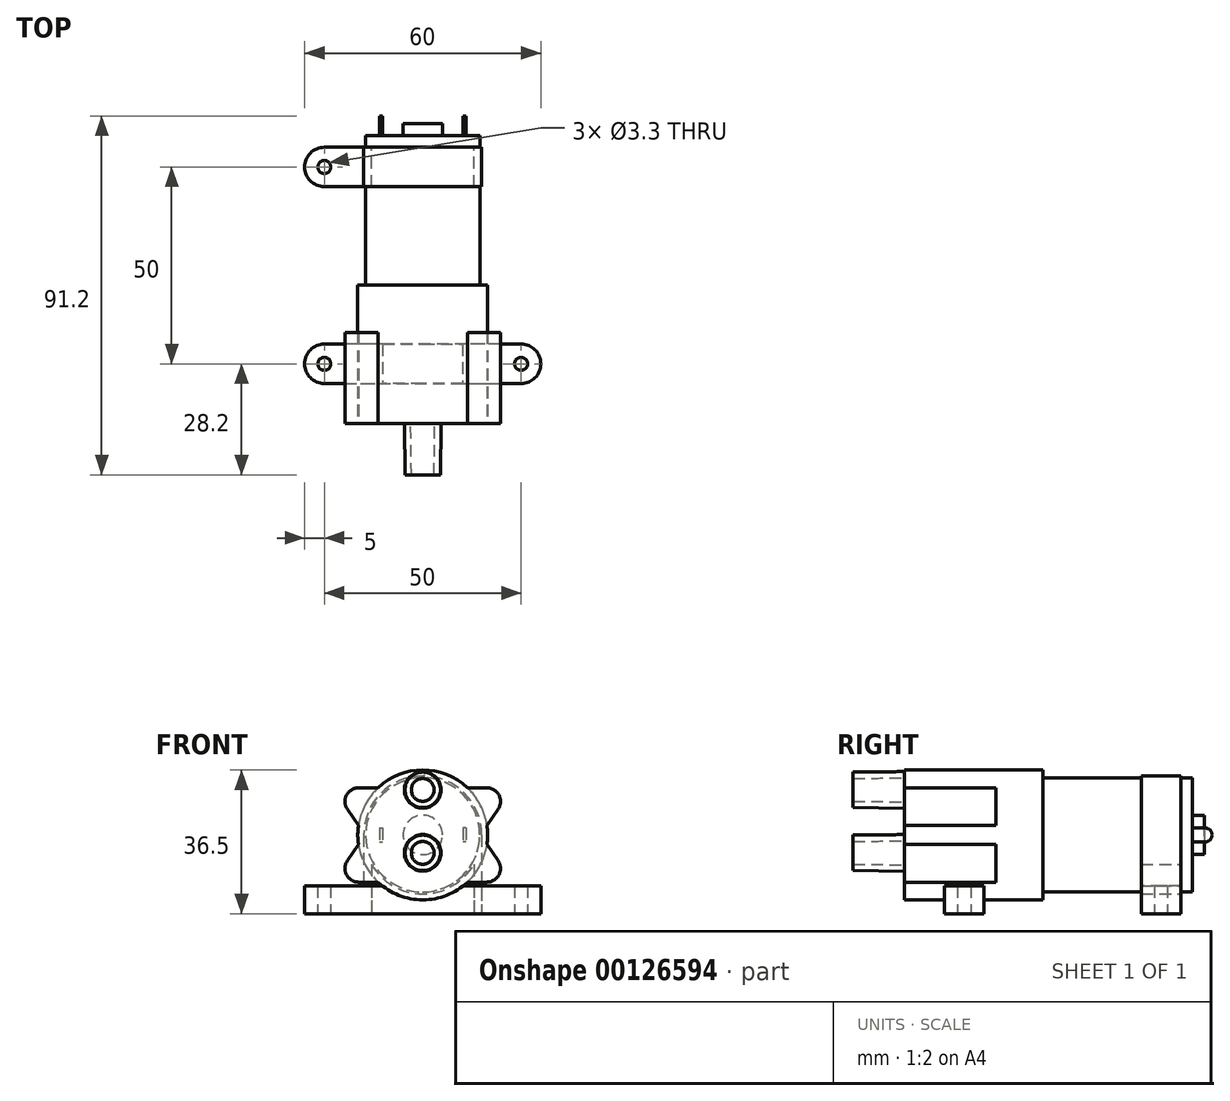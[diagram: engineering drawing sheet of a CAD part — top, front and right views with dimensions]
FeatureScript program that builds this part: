
annotation { "Feature Type Name" : "Feature", "Feature Type Description" : "" }
export const myFeature = defineFeature(function(context is Context, id is Id, definition is map)
    precondition{}
    {
        {
            var Q0;
            Q0=qCreatedBy(makeId("Front.planeOp"),FACE);
            var sketch = newSketch(context, id + "F0", { "sketchPlane" : qUnion([Q0])});
            skCircle(sketch, "E0", {"center": v(0, 0) * mm, "radius": 16.5 * mm});
            skCircle(sketch, "E1", {"center": v(16.25, -8.5) * mm, "radius": 3.5 * mm});
            skCircle(sketch, "E2.0.1.0", {"center": v(16.25, 8.5) * mm, "radius": 3.5 * mm});
            skCircle(sketch, "E2.1.0.0", {"center": v(-16.25, -8.5) * mm, "radius": 3.5 * mm});
            skCircle(sketch, "E2.1.1.0", {"center": v(-16.25, 8.5) * mm, "radius": 3.5 * mm});
            skLineSegment(sketch, "E2.direction1", {"start": v(16.25, -8.5) * mm, "end": v(-16.25, -8.5) * mm, "construction": true});
            skLineSegment(sketch, "E2.direction2", {"start": v(16.25, -8.5) * mm, "end": v(16.25, 8.5) * mm, "construction": true});
            skLineSegment(sketch, "E3", {"start": v(16.25, -8.5) * mm, "end": v(-16.25, 8.5) * mm, "construction": true});
            skLineSegment(sketch, "E4", {"start": v(16.25, 8.5) * mm, "end": v(-16.25, -8.5) * mm, "construction": true});
            skLineSegment(sketch, "E5", {"start": v(16.25, -12) * mm, "end": v(-16.25, -12) * mm});
            skLineSegment(sketch, "E6.MirrorCS", {"start": v(19.12, -6.5) * mm, "end": v(16.25, -2.36) * mm});
            skLineSegment(sketch, "E7.MirrorCS", {"start": v(-19.12, -6.5) * mm, "end": v(-16.25, -2.36) * mm});
            skLineSegment(sketch, "E8.MirrorCS", {"start": v(-19.12, 6.5) * mm, "end": v(-16.25, 2.36) * mm});
            skLineSegment(sketch, "E9.MirrorCS", {"start": v(19.12, 6.5) * mm, "end": v(16.25, 2.36) * mm});
            skLineSegment(sketch, "E10.MirrorCS", {"start": v(16.25, 12) * mm, "end": v(-16.25, 12) * mm});
            skSolve(sketch);
        }
        {
            var Q0;
            {var subQ0=sQuery(id+"F0.wireOp",EDGE,"E0");var subQ16=makeQuery(id+"F0.imprint","INTERSECT",VERTEX,{"derivedFrom":[subQ0,sQuery(id+"F0.wireOp",EDGE,"E9.MirrorCS")]});Q0=makeQuery(id+"F0.imprint","IMPRINT",FACE,{"disambiguationData":[TD([[makeQuery(id+"F0.imprint","IMPRINT",EDGE,{"disambiguationData":[TD([[subQ16,-1.0]])],"derivedFrom":subQ0}),1.0]])]});}
            var Q1;
            {var subQ0=sQuery(id+"F0.wireOp",EDGE,"E10.MirrorCS");var subQ1=sQuery(id+"F0.wireOp",EDGE,"E0");var subQ2=makeQuery(id+"F0.imprint","INTERSECT",VERTEX,{"disambiguationData":[OD(0.0)],"derivedFrom":[subQ1,subQ0]});Q1=makeQuery(id+"F0.imprint","IMPRINT",FACE,{"disambiguationData":[TD([[makeQuery(id+"F0.imprint","IMPRINT",EDGE,{"disambiguationData":[TD([[subQ2,1.0]])],"derivedFrom":subQ1}),-1.0]])]});}
            var Q2;
            {var subQ0=sQuery(id+"F0.wireOp",EDGE,"E2.1.1.0");var subQ1=sQuery(id+"F0.wireOp",EDGE,"E0");var subQ2=makeQuery(id+"F0.imprint","INTERSECT",VERTEX,{"disambiguationData":[OD(0.0)],"derivedFrom":[subQ1,subQ0]});Q2=makeQuery(id+"F0.imprint","IMPRINT",FACE,{"disambiguationData":[TD([[makeQuery(id+"F0.imprint","IMPRINT",EDGE,{"disambiguationData":[TD([[subQ2,-1.0]])],"derivedFrom":subQ1}),1.0]])]});}
            var Q3;
            {var subQ0=sQuery(id+"F0.wireOp",EDGE,"E2.1.1.0");var subQ1=sQuery(id+"F0.wireOp",EDGE,"E0");var subQ2=makeQuery(id+"F0.imprint","INTERSECT",VERTEX,{"disambiguationData":[OD(0.0)],"derivedFrom":[subQ1,subQ0]});Q3=makeQuery(id+"F0.imprint","IMPRINT",FACE,{"disambiguationData":[TD([[makeQuery(id+"F0.imprint","IMPRINT",EDGE,{"disambiguationData":[TD([[subQ2,-1.0]])],"derivedFrom":subQ1}),-1.0]])]});}
            var Q4;
            {var subQ0=sQuery(id+"F0.wireOp",EDGE,"E5");var subQ1=sQuery(id+"F0.wireOp",EDGE,"E0");var subQ2=makeQuery(id+"F0.imprint","INTERSECT",VERTEX,{"disambiguationData":[OD(0.0)],"derivedFrom":[subQ1,subQ0]});Q4=makeQuery(id+"F0.imprint","IMPRINT",FACE,{"disambiguationData":[TD([[makeQuery(id+"F0.imprint","IMPRINT",EDGE,{"disambiguationData":[TD([[subQ2,1.0]])],"derivedFrom":subQ1}),-1.0]])]});}
            var Q5;
            {var subQ0=sQuery(id+"F0.wireOp",EDGE,"E10.MirrorCS");var subQ1=sQuery(id+"F0.wireOp",EDGE,"E0");var subQ2=makeQuery(id+"F0.imprint","INTERSECT",VERTEX,{"disambiguationData":[OD(0.0)],"derivedFrom":[subQ1,subQ0]});Q5=makeQuery(id+"F0.imprint","IMPRINT",FACE,{"disambiguationData":[TD([[makeQuery(id+"F0.imprint","IMPRINT",EDGE,{"disambiguationData":[TD([[subQ2,-1.0]])],"derivedFrom":subQ1}),1.0]])]});}
            var Q6;
            {var subQ0=sQuery(id+"F0.wireOp",EDGE,"E6.MirrorCS");var subQ1=sQuery(id+"F0.wireOp",EDGE,"E0");var subQ2=makeQuery(id+"F0.imprint","INTERSECT",VERTEX,{"derivedFrom":[subQ1,subQ0]});Q6=makeQuery(id+"F0.imprint","IMPRINT",FACE,{"disambiguationData":[TD([[makeQuery(id+"F0.imprint","IMPRINT",EDGE,{"disambiguationData":[TD([[subQ2,1.0]])],"derivedFrom":subQ1}),-1.0]])]});}
            var Q7;
            {var subQ0=sQuery(id+"F0.wireOp",EDGE,"E2.0.1.0");var subQ1=sQuery(id+"F0.wireOp",EDGE,"E0");var subQ2=makeQuery(id+"F0.imprint","INTERSECT",VERTEX,{"disambiguationData":[OD(0.0)],"derivedFrom":[subQ1,subQ0]});Q7=makeQuery(id+"F0.imprint","IMPRINT",FACE,{"disambiguationData":[TD([[makeQuery(id+"F0.imprint","IMPRINT",EDGE,{"disambiguationData":[TD([[subQ2,-1.0]])],"derivedFrom":subQ1}),-1.0]])]});}
            var Q8;
            {var subQ0=sQuery(id+"F0.wireOp",EDGE,"E2.1.0.0");var subQ1=sQuery(id+"F0.wireOp",EDGE,"E0");var subQ2=makeQuery(id+"F0.imprint","INTERSECT",VERTEX,{"disambiguationData":[OD(0.0)],"derivedFrom":[subQ1,subQ0]});Q8=makeQuery(id+"F0.imprint","IMPRINT",FACE,{"disambiguationData":[TD([[makeQuery(id+"F0.imprint","IMPRINT",EDGE,{"disambiguationData":[TD([[subQ2,-1.0]])],"derivedFrom":subQ1}),-1.0]])]});}
            var Q9;
            {var subQ0=sQuery(id+"F0.wireOp",EDGE,"E5");var subQ1=sQuery(id+"F0.wireOp",EDGE,"E0");var subQ2=makeQuery(id+"F0.imprint","INTERSECT",VERTEX,{"disambiguationData":[OD(1.0)],"derivedFrom":[subQ1,subQ0]});Q9=makeQuery(id+"F0.imprint","IMPRINT",FACE,{"disambiguationData":[TD([[makeQuery(id+"F0.imprint","IMPRINT",EDGE,{"disambiguationData":[TD([[subQ2,-1.0]])],"derivedFrom":subQ1}),-1.0]])]});}
            var Q10;
            {var subQ0=sQuery(id+"F0.wireOp",EDGE,"E1");var subQ1=sQuery(id+"F0.wireOp",EDGE,"E0");var subQ2=makeQuery(id+"F0.imprint","INTERSECT",VERTEX,{"disambiguationData":[OD(0.0)],"derivedFrom":[subQ1,subQ0]});Q10=makeQuery(id+"F0.imprint","IMPRINT",FACE,{"disambiguationData":[TD([[makeQuery(id+"F0.imprint","IMPRINT",EDGE,{"disambiguationData":[TD([[subQ2,-1.0]])],"derivedFrom":subQ1}),-1.0]])]});}
            var Q11;
            {var subQ0=sQuery(id+"F0.wireOp",EDGE,"E10.MirrorCS");var subQ1=sQuery(id+"F0.wireOp",EDGE,"E0");var subQ2=makeQuery(id+"F0.imprint","INTERSECT",VERTEX,{"disambiguationData":[OD(1.0)],"derivedFrom":[subQ1,subQ0]});Q11=makeQuery(id+"F0.imprint","IMPRINT",FACE,{"disambiguationData":[TD([[makeQuery(id+"F0.imprint","IMPRINT",EDGE,{"disambiguationData":[TD([[subQ2,-1.0]])],"derivedFrom":subQ1}),-1.0]])]});}
            var Q12;
            {var subQ0=sQuery(id+"F0.wireOp",EDGE,"E9.MirrorCS");var subQ1=sQuery(id+"F0.wireOp",EDGE,"E0");var subQ2=makeQuery(id+"F0.imprint","INTERSECT",VERTEX,{"derivedFrom":[subQ1,subQ0]});Q12=makeQuery(id+"F0.imprint","IMPRINT",FACE,{"disambiguationData":[TD([[makeQuery(id+"F0.imprint","IMPRINT",EDGE,{"disambiguationData":[TD([[subQ2,-1.0]])],"derivedFrom":subQ1}),-1.0]])]});}
            var Q13;
            {var subQ0=sQuery(id+"F0.wireOp",EDGE,"E2.0.1.0");var subQ1=sQuery(id+"F0.wireOp",EDGE,"E0");var subQ2=makeQuery(id+"F0.imprint","INTERSECT",VERTEX,{"disambiguationData":[OD(0.0)],"derivedFrom":[subQ1,subQ0]});Q13=makeQuery(id+"F0.imprint","IMPRINT",FACE,{"disambiguationData":[TD([[makeQuery(id+"F0.imprint","IMPRINT",EDGE,{"disambiguationData":[TD([[subQ2,-1.0]])],"derivedFrom":subQ1}),1.0]])]});}
            var Q14;
            {var subQ0=sQuery(id+"F0.wireOp",EDGE,"E1");var subQ1=sQuery(id+"F0.wireOp",EDGE,"E0");var subQ2=makeQuery(id+"F0.imprint","INTERSECT",VERTEX,{"disambiguationData":[OD(0.0)],"derivedFrom":[subQ1,subQ0]});Q14=makeQuery(id+"F0.imprint","IMPRINT",FACE,{"disambiguationData":[TD([[makeQuery(id+"F0.imprint","IMPRINT",EDGE,{"disambiguationData":[TD([[subQ2,-1.0]])],"derivedFrom":subQ1}),1.0]])]});}
            var Q15;
            {var subQ0=sQuery(id+"F0.wireOp",EDGE,"E7.MirrorCS");var subQ1=sQuery(id+"F0.wireOp",EDGE,"E0");var subQ2=makeQuery(id+"F0.imprint","INTERSECT",VERTEX,{"derivedFrom":[subQ1,subQ0]});Q15=makeQuery(id+"F0.imprint","IMPRINT",FACE,{"disambiguationData":[TD([[makeQuery(id+"F0.imprint","IMPRINT",EDGE,{"disambiguationData":[TD([[subQ2,-1.0]])],"derivedFrom":subQ1}),-1.0]])]});}
            var Q16;
            {var subQ0=sQuery(id+"F0.wireOp",EDGE,"E2.1.0.0");var subQ1=sQuery(id+"F0.wireOp",EDGE,"E0");var subQ2=makeQuery(id+"F0.imprint","INTERSECT",VERTEX,{"disambiguationData":[OD(0.0)],"derivedFrom":[subQ1,subQ0]});Q16=makeQuery(id+"F0.imprint","IMPRINT",FACE,{"disambiguationData":[TD([[makeQuery(id+"F0.imprint","IMPRINT",EDGE,{"disambiguationData":[TD([[subQ2,-1.0]])],"derivedFrom":subQ1}),1.0]])]});}
            var Q17;
            {var subQ0=sQuery(id+"F0.wireOp",EDGE,"E8.MirrorCS");var subQ1=sQuery(id+"F0.wireOp",EDGE,"E0");var subQ2=makeQuery(id+"F0.imprint","INTERSECT",VERTEX,{"derivedFrom":[subQ1,subQ0]});Q17=makeQuery(id+"F0.imprint","IMPRINT",FACE,{"disambiguationData":[TD([[makeQuery(id+"F0.imprint","IMPRINT",EDGE,{"disambiguationData":[TD([[subQ2,1.0]])],"derivedFrom":subQ1}),-1.0]])]});}
            var Q18;
            {var subQ0=sQuery(id+"F0.wireOp",EDGE,"E5");var subQ1=sQuery(id+"F0.wireOp",EDGE,"E0");var subQ2=makeQuery(id+"F0.imprint","INTERSECT",VERTEX,{"disambiguationData":[OD(0.0)],"derivedFrom":[subQ1,subQ0]});Q18=makeQuery(id+"F0.imprint","IMPRINT",FACE,{"disambiguationData":[TD([[makeQuery(id+"F0.imprint","IMPRINT",EDGE,{"disambiguationData":[TD([[subQ2,-1.0]])],"derivedFrom":subQ1}),1.0]])]});}
            extrude(context, id + "F1", {"entities" : qUnion([Q0, Q1, Q2, Q3, Q4, Q5, Q6, Q7, Q8, Q9, Q10, Q11, Q12, Q13, Q14, Q15, Q16, Q17, Q18]), "oppositeDirection" : true, "depth" : 23.2 * mm, "offsetDistance" : 25 * mm});
        }
        {
            var Q0;
            Q0=qCreatedBy(makeId("Right.planeOp"),FACE);
            var sketch = newSketch(context, id + "F2", { "sketchPlane" : qUnion([Q0])});
            skLineSegment(sketch, "E11", {"start": v(0, 11.45) * mm, "end": v(-13, 11.45) * mm, "construction": true});
            skLineSegment(sketch, "E12", {"start": v(0, 16.1) * mm, "end": v(-13, 15.95) * mm});
            skLineSegment(sketch, "E13", {"start": v(-13, 15.95) * mm, "end": v(-12.98, 14.35) * mm});
            skLineSegment(sketch, "E14", {"start": v(-12.98, 14.35) * mm, "end": v(0, 14.5) * mm});
            skLineSegment(sketch, "E15", {"start": v(0, 16.1) * mm, "end": v(0, 14.5) * mm});
            skLineSegment(sketch, "E16.0.1.0", {"start": v(0, 0.1) * mm, "end": v(0, -1.5) * mm});
            skLineSegment(sketch, "E16.0.1.1", {"start": v(-12.98, -1.65) * mm, "end": v(0, -1.5) * mm});
            skLineSegment(sketch, "E16.0.1.2", {"start": v(0, 0.1) * mm, "end": v(-13, -0.05) * mm});
            skLineSegment(sketch, "E16.0.1.3", {"start": v(-13, -0.05) * mm, "end": v(-12.98, -1.65) * mm});
            skLineSegment(sketch, "E16.direction1", {"start": v(-12.98, 14.35) * mm, "end": v(12.02, 14.35) * mm, "construction": true});
            skLineSegment(sketch, "E16.direction2", {"start": v(-12.98, 14.35) * mm, "end": v(-12.98, -1.65) * mm, "construction": true});
            skLineSegment(sketch, "E17.0.1.0", {"start": v(0, -4.55) * mm, "end": v(-13, -4.55) * mm, "construction": true});
            skLineSegment(sketch, "E17.direction1", {"start": v(-13, 11.45) * mm, "end": v(12, 11.45) * mm, "construction": true});
            skLineSegment(sketch, "E17.direction2", {"start": v(-13, 11.45) * mm, "end": v(-13, -4.55) * mm, "construction": true});
            skSolve(sketch);
        }
        {
            var Q0;
            Q0=makeQuery(id+"F2.imprint","IMPRINT",FACE,{"disambiguationData":[TD([[makeQuery(id+"F2.imprint","IMPRINT",EDGE,{"derivedFrom":sQuery(id+"F2.wireOp",EDGE,"E12")}),1.0]])]});
            var Q1;
            Q1=sQuery(id+"F2.wireOp",EDGE,"E11");
            revolve(context, id + "F3", {"operationType" : NewBodyOperationType.ADD, "surfaceOperationType" : NewSurfaceOperationType.NEW, "entities" : qUnion([Q0]), "axis" : qUnion([Q1]), "revolveType" : RevolveType.FULL});
        }
        {
            var Q0;
            Q0=makeQuery(id+"F2.imprint","IMPRINT",FACE,{"disambiguationData":[TD([[makeQuery(id+"F2.imprint","IMPRINT",EDGE,{"derivedFrom":sQuery(id+"F2.wireOp",EDGE,"E16.0.1.0")}),-1.0]])]});
            var Q1;
            Q1=sQuery(id+"F2.wireOp",EDGE,"E17.0.1.0");
            revolve(context, id + "F4", {"operationType" : NewBodyOperationType.ADD, "surfaceOperationType" : NewSurfaceOperationType.NEW, "entities" : qUnion([Q0]), "axis" : qUnion([Q1]), "revolveType" : RevolveType.FULL});
        }
        {
            var Q0;
            Q0=makeQuery(id+"F1.opExtrude","CAP_FACE",FACE,{"disambiguationData":[OSD([sQuery(id+"F0.wireOp",EDGE,"E0"),sQuery(id+"F0.wireOp",EDGE,"E1"),sQuery(id+"F0.wireOp",EDGE,"E2.0.1.0"),sQuery(id+"F0.wireOp",EDGE,"E2.1.0.0"),sQuery(id+"F0.wireOp",EDGE,"E2.1.1.0"),sQuery(id+"F0.wireOp",EDGE,"E5"),sQuery(id+"F0.wireOp",EDGE,"E6.MirrorCS"),sQuery(id+"F0.wireOp",EDGE,"E7.MirrorCS"),sQuery(id+"F0.wireOp",EDGE,"E8.MirrorCS"),sQuery(id+"F0.wireOp",EDGE,"E9.MirrorCS"),sQuery(id+"F0.wireOp",EDGE,"E10.MirrorCS")])],"isStart":false});
            var sketch = newSketch(context, id + "F5", { "sketchPlane" : qUnion([Q0])});
            skCircle(sketch, "E18", {"center": v(0, 0) * mm, "radius": 16.5 * mm});
            skSolve(sketch);
        }
        {
            var Q0;
            {var subQ0=sQuery(id+"F5.wireOp",EDGE,"E18");var subQ1=makeQuery(id+"F5.imprint","INTERSECT",VERTEX,{"derivedFrom":[makeQuery(id+"F1.opExtrude","CAP_EDGE",EDGE,{"disambiguationData":[OSD([sQuery(id+"F0.wireOp",EDGE,"E8.MirrorCS")])],"isStart":false}),subQ0]});var subQ2=makeQuery(id+"F5.imprint","INTERSECT",VERTEX,{"derivedFrom":[makeQuery(id+"F1.opExtrude","CAP_EDGE",EDGE,{"disambiguationData":[OSD([sQuery(id+"F0.wireOp",EDGE,"E7.MirrorCS")])],"isStart":false}),subQ0]});Q0=makeQuery(id+"F5.imprint","IMPRINT",FACE,{"disambiguationData":[TD([[makeQuery(id+"F5.imprint","IMPRINT",EDGE,{"disambiguationData":[TD([[subQ1,-1.0],[subQ2,1.0]])],"derivedFrom":subQ0}),-1.0]])]});}
            extrude(context, id + "F6", {"entities" : qUnion([Q0]), "operationType" : NewBodyOperationType.ADD, "depth" : 12 * mm, "offsetDistance" : 25 * mm});
        }
        {
            var Q0;
            Q0=makeQuery(id+"F6.opExtrude","CAP_FACE",FACE,{"disambiguationData":[OSD([sQuery(id+"F5.wireOp",EDGE,"E18")])],"isStart":false});
            var sketch = newSketch(context, id + "F7", { "sketchPlane" : qUnion([Q0])});
            skCircle(sketch, "E19", {"center": v(0, 0) * mm, "radius": 14.5 * mm});
            skSolve(sketch);
        }
        {
            var Q0;
            Q0=makeQuery(id+"F7.imprint","IMPRINT",FACE,{"disambiguationData":[TD([[makeQuery(id+"F7.imprint","IMPRINT",EDGE,{"derivedFrom":sQuery(id+"F7.wireOp",EDGE,"E19")}),1.0]])]});
            extrude(context, id + "F8", {"entities" : qUnion([Q0]), "operationType" : NewBodyOperationType.ADD, "depth" : 38 * mm, "offsetDistance" : 25 * mm});
        }
        {
            var Q0;
            Q0=makeQuery(id+"F8.opExtrude","CAP_FACE",FACE,{"disambiguationData":[OSD([sQuery(id+"F7.wireOp",EDGE,"E19")])],"isStart":false});
            var sketch = newSketch(context, id + "F9", { "sketchPlane" : qUnion([Q0])});
            skCircle(sketch, "E20", {"center": v(0, 0) * mm, "radius": 5 * mm});
            skLineSegment(sketch, "E21.bottom", {"start": v(-11, 1.75) * mm, "end": v(-10.2, 1.75) * mm});
            skLineSegment(sketch, "E21.top", {"start": v(-11, -1.75) * mm, "end": v(-10.2, -1.75) * mm});
            skLineSegment(sketch, "E21.left", {"start": v(-11, 1.75) * mm, "end": v(-11, -1.75) * mm});
            skLineSegment(sketch, "E21.right", {"start": v(-10.2, 1.75) * mm, "end": v(-10.2, -1.75) * mm});
            skLineSegment(sketch, "E22.MirrorCS", {"start": v(10.2, 1.75) * mm, "end": v(10.2, -1.75) * mm});
            skLineSegment(sketch, "E23.MirrorCS", {"start": v(11, 1.75) * mm, "end": v(11, -1.75) * mm});
            skLineSegment(sketch, "E24.MirrorCS", {"start": v(11, 1.75) * mm, "end": v(10.2, 1.75) * mm});
            skLineSegment(sketch, "E25.MirrorCS", {"start": v(11, -1.75) * mm, "end": v(10.2, -1.75) * mm});
            skSolve(sketch);
        }
        {
            var Q0;
            Q0=makeQuery(id+"F9.imprint","IMPRINT",FACE,{"disambiguationData":[TD([[makeQuery(id+"F9.imprint","IMPRINT",EDGE,{"derivedFrom":sQuery(id+"F9.wireOp",EDGE,"E20")}),1.0]])]});
            extrude(context, id + "F10", {"entities" : qUnion([Q0]), "operationType" : NewBodyOperationType.ADD, "depth" : 3 * mm, "offsetDistance" : 25 * mm});
        }
        {
            var Q0;
            Q0=makeQuery(id+"F9.imprint","IMPRINT",FACE,{"disambiguationData":[TD([[makeQuery(id+"F9.imprint","IMPRINT",EDGE,{"derivedFrom":sQuery(id+"F9.wireOp",EDGE,"E21.bottom")}),-1.0]])]});
            var Q1;
            Q1=makeQuery(id+"F9.imprint","IMPRINT",FACE,{"disambiguationData":[TD([[makeQuery(id+"F9.imprint","IMPRINT",EDGE,{"derivedFrom":sQuery(id+"F9.wireOp",EDGE,"E22.MirrorCS")}),1.0]])]});
            extrude(context, id + "F11", {"entities" : qUnion([Q0, Q1]), "operationType" : NewBodyOperationType.ADD, "depth" : 5 * mm, "offsetDistance" : 25 * mm});
        }
        {
            var Q0;
            Q0=makeQuery(id+"F11.opExtrude","CAP_EDGE",EDGE,{"disambiguationData":[OSD([sQuery(id+"F9.wireOp",EDGE,"E25.MirrorCS")])],"isStart":false});
            var Q1;
            Q1=makeQuery(id+"F11.opExtrude","CAP_EDGE",EDGE,{"disambiguationData":[OSD([sQuery(id+"F9.wireOp",EDGE,"E24.MirrorCS")])],"isStart":false});
            var Q2;
            Q2=makeQuery(id+"F11.opExtrude","CAP_EDGE",EDGE,{"disambiguationData":[OSD([sQuery(id+"F9.wireOp",EDGE,"E21.top")])],"isStart":false});
            var Q3;
            Q3=makeQuery(id+"F11.opExtrude","CAP_EDGE",EDGE,{"disambiguationData":[OSD([sQuery(id+"F9.wireOp",EDGE,"E21.bottom")])],"isStart":false});
            fillet(context, id + "F12", {"entities" : qUnion([Q0, Q1, Q2, Q3]), "radius" : (3.5 / 2) * mm, "tangentPropagation" : true, "allowEdgeOverflow" : false});
        }
        {
            var Q0;
            Q0=qCreatedBy(makeId("Top.planeOp"),FACE);
            cPlane(context, id + "F13", {"entities" : qUnion([Q0]), "cplaneType" : CPlaneType.OFFSET, "offset" : 20 * mm, "oppositeDirection" : true, "width" : 150 * mm, "height" : 150 * mm});
        }
        {
            var Q0;
            Q0=qCreatedBy(id+"F13.planeOp",FACE);
            var sketch = newSketch(context, id + "F14", { "sketchPlane" : qUnion([Q0])});
            skCircle(sketch, "E26", {"center": v(-25, 15.2) * mm, "radius": 1.65 * mm});
            skCircle(sketch, "E27.0.1.0", {"center": v(-25, 65.2) * mm, "radius": 1.65 * mm});
            skLineSegment(sketch, "E27.direction1", {"start": v(-25, 15.2) * mm, "end": v(25, 15.2) * mm, "construction": true});
            skLineSegment(sketch, "E27.direction2", {"start": v(-25, 15.2) * mm, "end": v(-25, 65.2) * mm, "construction": true});
            skLineSegment(sketch, "E28", {"start": v(-25, 10.2) * mm, "end": v(25, 10.2) * mm});
            skLineSegment(sketch, "E29", {"start": v(25, 20.2) * mm, "end": v(-25, 20.2) * mm});
            skArc(sketch, "E30", {"start": v(-25, 20.2) * mm, "mid": v(-30, 15.2) * mm, "end": v(-25, 10.2) * mm});
            skArc(sketch, "E31", {"start": v(25, 20.2) * mm, "mid": v(30, 15.2) * mm, "end": v(25, 10.2) * mm});
            skLineSegment(sketch, "E32.0.1.0", {"start": v(-25, 60.2) * mm, "end": v(25, 60.2) * mm});
            skArc(sketch, "E32.0.1.1", {"start": v(25, 70.2) * mm, "mid": v(30, 65.2) * mm, "end": v(25, 60.2) * mm});
            skLineSegment(sketch, "E32.0.1.2", {"start": v(25, 70.2) * mm, "end": v(-25, 70.2) * mm});
            skArc(sketch, "E32.0.1.3", {"start": v(-25, 70.2) * mm, "mid": v(-30, 65.2) * mm, "end": v(-25, 60.2) * mm});
            skLineSegment(sketch, "E32.direction1", {"start": v(-25, 10.2) * mm, "end": v(0, 10.2) * mm, "construction": true});
            skLineSegment(sketch, "E32.direction2", {"start": v(-25, 10.2) * mm, "end": v(-25, 60.2) * mm, "construction": true});
            skCircle(sketch, "E33", {"center": v(25, 65.2) * mm, "radius": 1.65 * mm});
            skCircle(sketch, "E34", {"center": v(25, 15.2) * mm, "radius": 1.65 * mm});
            skLineSegment(sketch, "E35", {"start": v(-13, 60.2) * mm, "end": v(-13, 70.2) * mm});
            skLineSegment(sketch, "E36", {"start": v(13, 60.2) * mm, "end": v(13, 70.2) * mm});
            skLineSegment(sketch, "E37", {"start": v(-15, 60.2) * mm, "end": v(-15, 70.2) * mm});
            skLineSegment(sketch, "E38.MirrorCS", {"start": v(15, 60.2) * mm, "end": v(15, 70.2) * mm});
            skSolve(sketch);
        }
        {
            var Q0;
            Q0=makeQuery(id+"F14.imprint","IMPRINT",FACE,{"disambiguationData":[TD([[makeQuery(id+"F14.imprint","IMPRINT",EDGE,{"derivedFrom":sQuery(id+"F14.wireOp",EDGE,"E26")}),-1.0]])]});
            extrude(context, id + "F15", {"entities" : qUnion([Q0]), "operationType" : NewBodyOperationType.ADD, "depth" : 7 * mm, "offsetDistance" : 25 * mm});
        }
        {
            var Q0;
            {var subQ0=sQuery(id+"F14.wireOp",EDGE,"E35");Q0=makeQuery(id+"F14.imprint","IMPRINT",FACE,{"disambiguationData":[TD([[makeQuery(id+"F14.imprint","IMPRINT",EDGE,{"derivedFrom":subQ0}),1.0]])]});}
            var Q1;
            {var subQ0=sQuery(id+"F14.wireOp",EDGE,"E36");Q1=makeQuery(id+"F14.imprint","IMPRINT",FACE,{"disambiguationData":[TD([[makeQuery(id+"F14.imprint","IMPRINT",EDGE,{"derivedFrom":subQ0}),-1.0]])]});}
            extrude(context, id + "F16", {"entities" : qUnion([Q0, Q1]), "operationType" : NewBodyOperationType.ADD, "depth" : 20 * mm, "offsetDistance" : 25 * mm});
        }
        {
            var Q0;
            Q0=makeQuery(id+"F14.imprint","IMPRINT",FACE,{"disambiguationData":[TD([[makeQuery(id+"F14.imprint","IMPRINT",EDGE,{"derivedFrom":sQuery(id+"F14.wireOp",EDGE,"E27.0.1.0")}),-1.0]])]});
            var Q1;
            {var subQ1=sQuery(id+"F14.wireOp",EDGE,"E32.0.1.1");Q1=makeQuery(id+"F14.imprint","IMPRINT",FACE,{"disambiguationData":[TD([[makeQuery(id+"F14.imprint","IMPRINT",EDGE,{"derivedFrom":subQ1}),-1.0]])]});}
            extrude(context, id + "F17", {"entities" : qUnion([Q0, Q1]), "operationType" : NewBodyOperationType.ADD, "depth" : 7 * mm, "offsetDistance" : 25 * mm});
        }
        {
            var Q0;
            {var subQ0=sQuery(id+"F14.wireOp",EDGE,"E32.0.1.2");Q0=makeQuery(id+"F17.boolean.opBoolean","MERGE",FACE,{"derivedFrom":[makeQuery(id+"F16.opExtrude","SWEPT_FACE",FACE,{"disambiguationData":[OSD([subQ0]),TDD([makeQuery(id+"F14.imprint","IMPRINT",EDGE,{"disambiguationData":[TD([[makeQuery(id+"F14.imprint","INTERSECT",VERTEX,{"derivedFrom":[subQ0,sQuery(id+"F14.wireOp",EDGE,"E35")]}),-1.0]])],"derivedFrom":subQ0})])]}),makeQuery(id+"F17.opExtrude","SWEPT_FACE",FACE,{"disambiguationData":[OSD([subQ0]),TDD([makeQuery(id+"F14.imprint","IMPRINT",EDGE,{"disambiguationData":[TD([[makeQuery(id+"F14.imprint","INTERSECT",VERTEX,{"derivedFrom":[subQ0,sQuery(id+"F14.wireOp",EDGE,"E32.0.1.3")]}),1.0]])],"derivedFrom":subQ0})])]})]});}
            var sketch = newSketch(context, id + "F18", { "sketchPlane" : qUnion([Q0])});
            skCircle(sketch, "E39", {"center": v(0, 0) * mm, "radius": 15 * mm});
            skSolve(sketch);
        }
        {
            var Q0;
            {var subQ2=sQuery(id+"F14.wireOp",EDGE,"E32.0.1.2");var subQ3=sQuery(id+"F14.wireOp",EDGE,"E35");var subQ4=makeQuery(id+"F14.imprint","IMPRINT",EDGE,{"disambiguationData":[TD([[makeQuery(id+"F14.imprint","INTERSECT",VERTEX,{"derivedFrom":[subQ2,subQ3]}),-1.0]])],"derivedFrom":subQ2});var subQ5=makeQuery(id+"F16.opExtrude","CAP_EDGE",EDGE,{"disambiguationData":[OSD([subQ2]),TDD([subQ4])],"isStart":false});Q0=makeQuery(id+"F18.imprint","IMPRINT",FACE,{"disambiguationData":[TD([[makeQuery(id+"F18.imprint","IMPRINT",EDGE,{"derivedFrom":subQ5}),1.0]])]});}
            var Q1;
            {var subQ0=sQuery(id+"F14.wireOp",EDGE,"E32.0.1.0");Q1=makeQuery(id+"F17.boolean.opBoolean","MERGE",FACE,{"derivedFrom":[makeQuery(id+"F16.opExtrude","SWEPT_FACE",FACE,{"disambiguationData":[OSD([subQ0]),TDD([makeQuery(id+"F14.imprint","IMPRINT",EDGE,{"disambiguationData":[TD([[makeQuery(id+"F14.imprint","INTERSECT",VERTEX,{"derivedFrom":[subQ0,sQuery(id+"F14.wireOp",EDGE,"E36")]}),-1.0]])],"derivedFrom":subQ0})])]}),makeQuery(id+"F17.opExtrude","SWEPT_FACE",FACE,{"disambiguationData":[OSD([subQ0]),TDD([makeQuery(id+"F14.imprint","IMPRINT",EDGE,{"disambiguationData":[TD([[makeQuery(id+"F14.imprint","INTERSECT",VERTEX,{"derivedFrom":[subQ0,sQuery(id+"F14.wireOp",EDGE,"E32.0.1.1")]}),1.0]])],"derivedFrom":subQ0})])]})]});}
            extrude(context, id + "F19", {"entities" : qUnion([Q0]), "operationType" : NewBodyOperationType.ADD, "endBound" : BoundingType.UP_TO_SURFACE, "oppositeDirection" : true, "depth" : 25 * mm, "endBoundEntityFace" : qUnion([Q1]), "offsetDistance" : 25 * mm});
        }
    });
